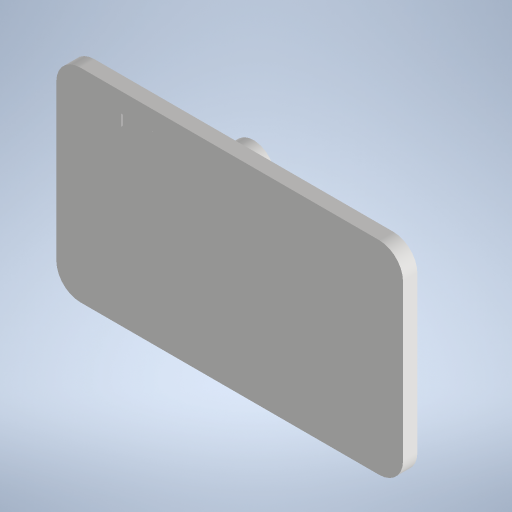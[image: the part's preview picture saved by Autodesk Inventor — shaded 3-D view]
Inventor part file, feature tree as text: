
AUTODESK INVENTOR PART (.ipt)
format: ipt  version: 2023 (Build 270158000, 158)  size: 316,928 bytes
history: native  units: mm
features: extrude x6, sketch x6, projected_geometry x3, other x2, fillet x2, chamfer x2, mirror x2
ambient origin geometry x8: Origin, YZ Plane, XZ Plane, XY Plane, X Axis, Y Axis, Z Axis, Center Point
bodies: Body1 (feature_tree)
feature tree (23):
  other  "솔리드1"
  extrude  "돌출1"  Depth=72.5mm
  extrude  "돌출2"  Depth=42.5mm
  fillet  "모깎기1"  Radius=3.0mm
  extrude  "돌출4"  Depth=4.5mm
  chamfer  "모따기1"  Distance=4.5mm
  other  "작업 평면1"
  extrude  "돌출5"  Depth=16.825mm
  mirror  "미러1"
  fillet  "모깎기2"  Radius=2.0mm
  extrude  "돌출6"  Depth=5.0mm
  extrude  "돌출7"  Depth=2.0mm
  chamfer  "모따기2"  Distance=45.0mm
  mirror  "미러2"
  sketch  "스케치1"
  sketch  "스케치2"
  projected_geometry  "투영된 루프1"
  sketch  "스케치5"
  sketch  "스케치6"
  sketch  "스케치7"
  projected_geometry  "투영된 루프3"
  projected_geometry  "투영된 루프4"
  sketch  "스케치8"
